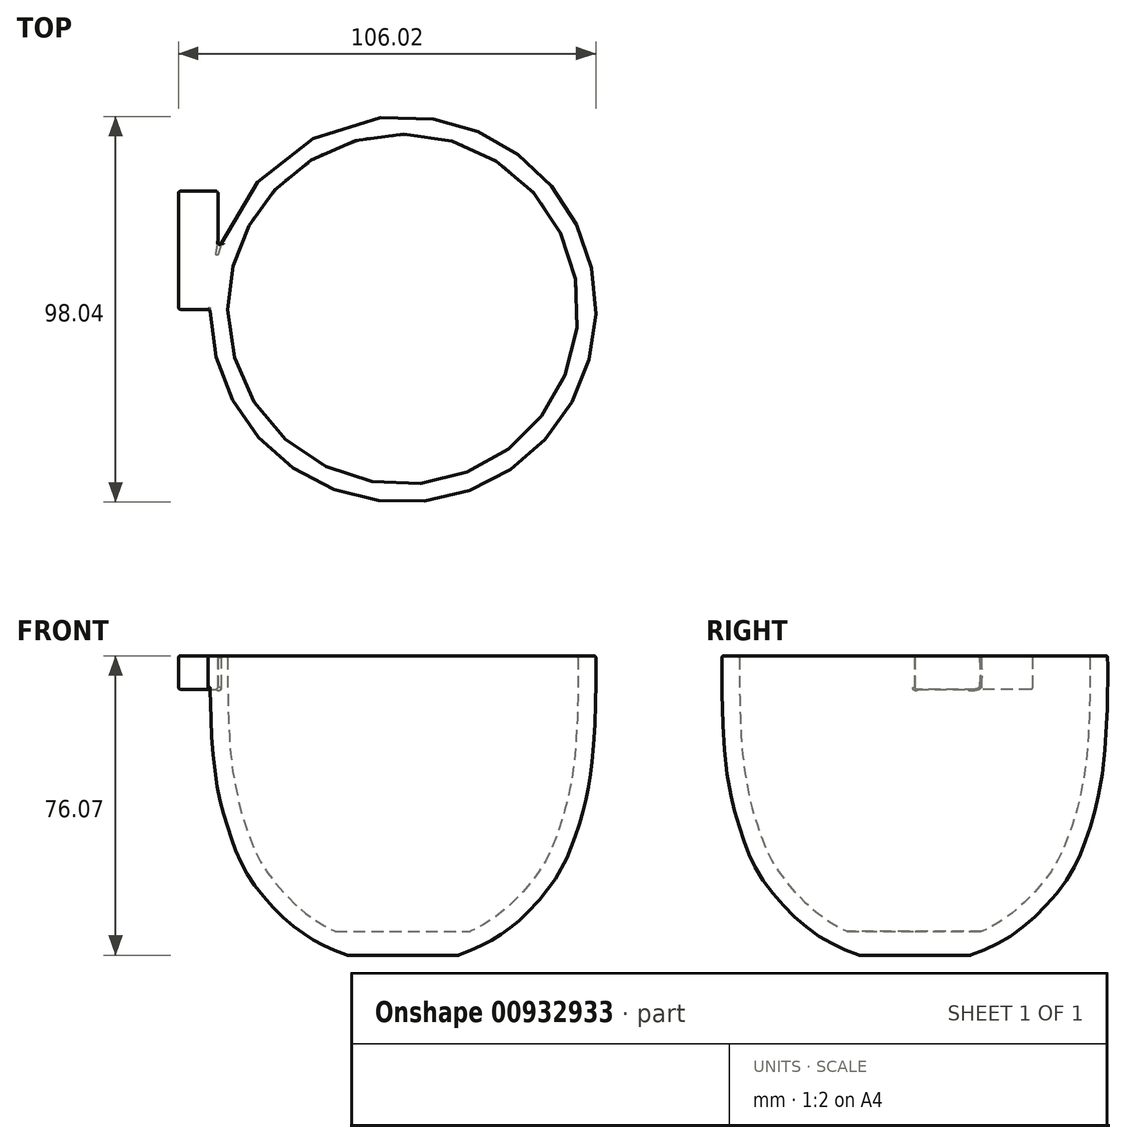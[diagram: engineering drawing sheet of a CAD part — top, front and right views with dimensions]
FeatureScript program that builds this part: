
annotation { "Feature Type Name" : "Feature", "Feature Type Description" : "" }
export const myFeature = defineFeature(function(context is Context, id is Id, definition is map)
    precondition{}
    {
        {
            var Q0;
            Q0=qCreatedBy(makeId("Front.planeOp"),FACE);
            var sketch = newSketch(context, id + "F0", { "sketchPlane" : qUnion([Q0])});
            skLineSegment(sketch, "E0", {"start": v(0, 78.82) * mm, "end": v(-49, 78.82) * mm});
            skLineSegment(sketch, "E1", {"start": v(0, 0) * mm, "end": v(0, 78.82) * mm});
            skFitSpline(sketch, "E2", {"points": [v(-49, 78.82) * mm, v(-49, 71.2) * mm, v(-47.95, 50.94) * mm, v(-44.24, 34.32) * mm, v(-38.54, 21.8) * mm, v(-27.37, 9.77) * mm, v(-17.3, 3.96) * mm, v(0, 0) * mm], "startDerivative": vector(-0.53, -120.05) * mm, "endDerivative": vector(126.32, 0) * mm});
            skSolve(sketch);
        }
        {
            var Q0;
            Q0=qSketchRegion(id+"F0",true);
            var Q1;
            Q1=sQuery(id+"F0.wireOp",EDGE,"E1");
            revolve(context, id + "F1", {"surfaceOperationType" : NewSurfaceOperationType.NEW, "entities" : qUnion([Q0]), "axis" : qUnion([Q1]), "revolveType" : RevolveType.FULL});
        }
        {
            var Q0;
            Q0=makeQuery(id+"F1.opRevolve","SWEPT_FACE",FACE,{"disambiguationData":[OSD([sQuery(id+"F0.wireOp",EDGE,"E0")])]});
            shell(context, id + "F2", {"entities" : qUnion([Q0]), "thickness" : 4.5 * mm});
        }
        {
            var Q0;
            Q0=qCreatedBy(makeId("Front.planeOp"),FACE);
            var sketch = newSketch(context, id + "F3", { "sketchPlane" : qUnion([Q0])});
            skLineSegment(sketch, "E3", {"start": v(-41.77, 30.38) * mm, "end": v(-53.43, 30.38) * mm});
            skLineSegment(sketch, "E4", {"start": v(-49.23, 20.12) * mm, "end": v(-36.53, 20.12) * mm});
            skLineSegment(sketch, "E5", {"start": v(-36.53, 20.12) * mm, "end": v(-41.77, 30.38) * mm});
            skFitSpline(sketch, "E6", {"points": [v(-42.03, 8) * mm, v(-47.44, 16.94) * mm, v(-49.23, 20.12) * mm, v(-51.33, 24.44) * mm, v(-53.43, 30.38) * mm, v(-55.23, 38.72) * mm, v(-56.67, 49.18) * mm, v(-57.32, 61.86) * mm, v(-57.58, 68.13) * mm, v(-57.6, 68.09) * mm], "startDerivative": vector(-47.1, 69.03) * mm, "endDerivative": vector(-6.03, -13.35) * mm});
            skLineSegment(sketch, "E7", {"start": v(-57.58, 68.13) * mm, "end": v(-69.83, 68.13) * mm});
            skFitSpline(sketch, "E8", {"points": [v(-69.83, 68.13) * mm, v(-69.83, 61.07) * mm, v(-69.06, 51.29) * mm, v(-67.63, 40.46) * mm, v(-65.54, 31.18) * mm, v(-63.64, 25) * mm, v(-58.64, 14.66) * mm, v(-54.3, 8) * mm], "startDerivative": vector(-1.12, -53.42) * mm, "endDerivative": vector(31.44, -44.67) * mm});
            skLineSegment(sketch, "E9", {"start": v(-54.3, 8) * mm, "end": v(-42.03, 8) * mm});
            skSolve(sketch);
        }
        {
            var Q0;
            Q0=qCreatedBy(makeId("Right.planeOp"),FACE);
            cPlane(context, id + "F4", {"entities" : qUnion([Q0]), "cplaneType" : CPlaneType.OFFSET, "offset" : 65 * mm, "oppositeDirection" : true, "width" : 150 * mm, "height" : 150 * mm});
        }
        {
            var Q0;
            Q0=qCreatedBy(id+"F4.planeOp",FACE);
            var sketch = newSketch(context, id + "F5", { "sketchPlane" : qUnion([Q0])});
            skPoint(sketch, "E10.middle", {"position": v(0, 24.44) * mm});
            skCircle(sketch, "E11", {"center": v(10, 68.82) * mm, "radius": 6 * mm});
            skSolve(sketch);
        }
        {
            var Q0;
            Q0=qCreatedBy(makeId("Top.planeOp"),FACE);
            cPlane(context, id + "F6", {"entities" : qUnion([Q0]), "cplaneType" : CPlaneType.OFFSET, "offset" : 8 * mm, "width" : 150 * mm, "height" : 150 * mm});
        }
        {
            var Q0;
            Q0=qCreatedBy(makeId("Front.planeOp"),FACE);
            var sketch = newSketch(context, id + "F7", { "sketchPlane" : qUnion([Q0])});
            skLineSegment(sketch, "E12", {"start": v(0, 1.35) * mm, "end": v(0, 8.85) * mm});
            skLineSegment(sketch, "E13", {"start": v(0, 8.85) * mm, "end": v(-21, 8.85) * mm});
            skLineSegment(sketch, "E14", {"start": v(-21, 8.85) * mm, "end": v(0, 1.35) * mm});
            skSolve(sketch);
        }
        {
            var Q0;
            Q0=qSketchRegion(id+"F7",true);
            var Q1;
            Q1=sQuery(id+"F7.wireOp",EDGE,"E12");
            revolve(context, id + "F8", {"operationType" : NewBodyOperationType.ADD, "surfaceOperationType" : NewSurfaceOperationType.NEW, "entities" : qUnion([Q0]), "axis" : qUnion([Q1]), "revolveType" : RevolveType.FULL});
        }
        {
            var Q0;
            Q0=qCreatedBy(makeId("Front.planeOp"),FACE);
            var sketch = newSketch(context, id + "F9", { "sketchPlane" : qUnion([Q0])});
            skLineSegment(sketch, "E15.bottom", {"start": v(20, 0) * mm, "end": v(-20, 0) * mm});
            skLineSegment(sketch, "E15.top", {"start": v(20, 2.75) * mm, "end": v(-20, 2.75) * mm});
            skLineSegment(sketch, "E15.left", {"start": v(20, 0) * mm, "end": v(20, 2.75) * mm});
            skLineSegment(sketch, "E15.right", {"start": v(-20, 0) * mm, "end": v(-20, 2.75) * mm});
            skSolve(sketch);
        }
        {
            var Q0;
            Q0=qSketchRegion(id+"F9",true);
            extrude(context, id + "F10", {"entities" : qUnion([Q0]), "operationType" : NewBodyOperationType.REMOVE, "oppositeDirection" : true, "depth" : 40 * mm, "offsetDistance" : 25 * mm, "symmetric" : true});
        }
        {
            var Q0;
            Q0=qCreatedBy(makeId("Front.planeOp"),FACE);
            var sketch = newSketch(context, id + "F11", { "sketchPlane" : qUnion([Q0])});
            skLineSegment(sketch, "E16", {"start": v(-47, 78.82) * mm, "end": v(-57, 78.82) * mm});
            skLineSegment(sketch, "E17", {"start": v(-57, 78.82) * mm, "end": v(-57, 70.32) * mm});
            skLineSegment(sketch, "E18", {"start": v(-57, 70.32) * mm, "end": v(-47, 70.32) * mm});
            skLineSegment(sketch, "E19", {"start": v(-47, 70.32) * mm, "end": v(-47, 78.82) * mm});
            skSolve(sketch);
        }
        {
            var Q0;
            Q0=makeQuery(id+"F11.imprint","IMPRINT",FACE,{"disambiguationData":[TD([[makeQuery(id+"F11.imprint","IMPRINT",EDGE,{"derivedFrom":sQuery(id+"F11.wireOp",EDGE,"E16")}),1.0]])]});
            extrude(context, id + "F12", {"entities" : qUnion([Q0]), "operationType" : NewBodyOperationType.ADD, "oppositeDirection" : true, "depth" : 30 * mm, "offsetDistance" : 25 * mm});
        }
        {
            var Q0;
            Q0=makeQuery(id+"F10.boolean.opBoolean","INTERSECT",EDGE,{"derivedFrom":[makeQuery(id+"F1.opRevolve","SWEPT_FACE",FACE,{"disambiguationData":[OSD([sQuery(id+"F0.wireOp",EDGE,"E2")])]}),makeQuery(id+"F10.opExtrude","SWEPT_FACE",FACE,{"disambiguationData":[OSD([sQuery(id+"F9.wireOp",EDGE,"E15.top")])]})]});
            var Q1;
            Q1=makeQuery(id+"F8.boolean.opBoolean","INTERSECT",EDGE,{"derivedFrom":[makeQuery(id+"F2.opShell","OFFSET_FACE",FACE,{"disambiguationData":[OSD([sQuery(id+"F0.wireOp",EDGE,"E2")])]}),makeQuery(id+"F8.opRevolve","SWEPT_FACE",FACE,{"disambiguationData":[OSD([sQuery(id+"F7.wireOp",EDGE,"E13")])]})]});
            var Q2;
            Q2=makeQuery(id+"FC7ZZsdAC91BJhE_1.boolean.opBoolean","MERGE",FACE,{"derivedFrom":[makeQuery(id+"F1.opRevolve","SWEPT_FACE",FACE,{"disambiguationData":[OSD([sQuery(id+"F0.wireOp",EDGE,"E0")])]}),makeQuery(id+"FC7ZZsdAC91BJhE_1.opRevolve","SWEPT_FACE",FACE,{"disambiguationData":[OSD([sQuery(id+"F11.wireOp",EDGE,"E16")])]})]});
            var Q3;
            Q3=makeQuery(id+"F12.opExtrude","CAP_FACE",FACE,{"disambiguationData":[OSD([sQuery(id+"F11.wireOp",EDGE,"E16"),sQuery(id+"F11.wireOp",EDGE,"E17"),sQuery(id+"F11.wireOp",EDGE,"E18"),sQuery(id+"F11.wireOp",EDGE,"E19")])],"isStart":true});
            var Q4;
            Q4=makeQuery(id+"F12.opExtrude","SWEPT_FACE",FACE,{"disambiguationData":[OSD([sQuery(id+"F11.wireOp",EDGE,"E17")])]});
            var Q5;
            Q5=makeQuery(id+"F12.opExtrude","CAP_FACE",FACE,{"disambiguationData":[OSD([sQuery(id+"F11.wireOp",EDGE,"E16"),sQuery(id+"F11.wireOp",EDGE,"E17"),sQuery(id+"F11.wireOp",EDGE,"E18"),sQuery(id+"F11.wireOp",EDGE,"E19")])],"isStart":false});
            var Q6;
            Q6=makeQuery(id+"F12.opExtrude","SWEPT_FACE",FACE,{"disambiguationData":[OSD([sQuery(id+"F11.wireOp",EDGE,"E19")])]});
            var Q7;
            Q7=makeQuery(id+"F12.opExtrude","SWEPT_FACE",FACE,{"disambiguationData":[OSD([sQuery(id+"F11.wireOp",EDGE,"E18")])]});
            fillet(context, id + "F13", {"entities" : qUnion([Q0, Q1, Q2, Q3, Q4, Q5, Q6, Q7]), "tangentPropagation" : true, "radius" : .5 * mm, "defaultsChanged" : false, "vertexSettings" : [], "allowEdgeOverflow" : false});
        }
    });
